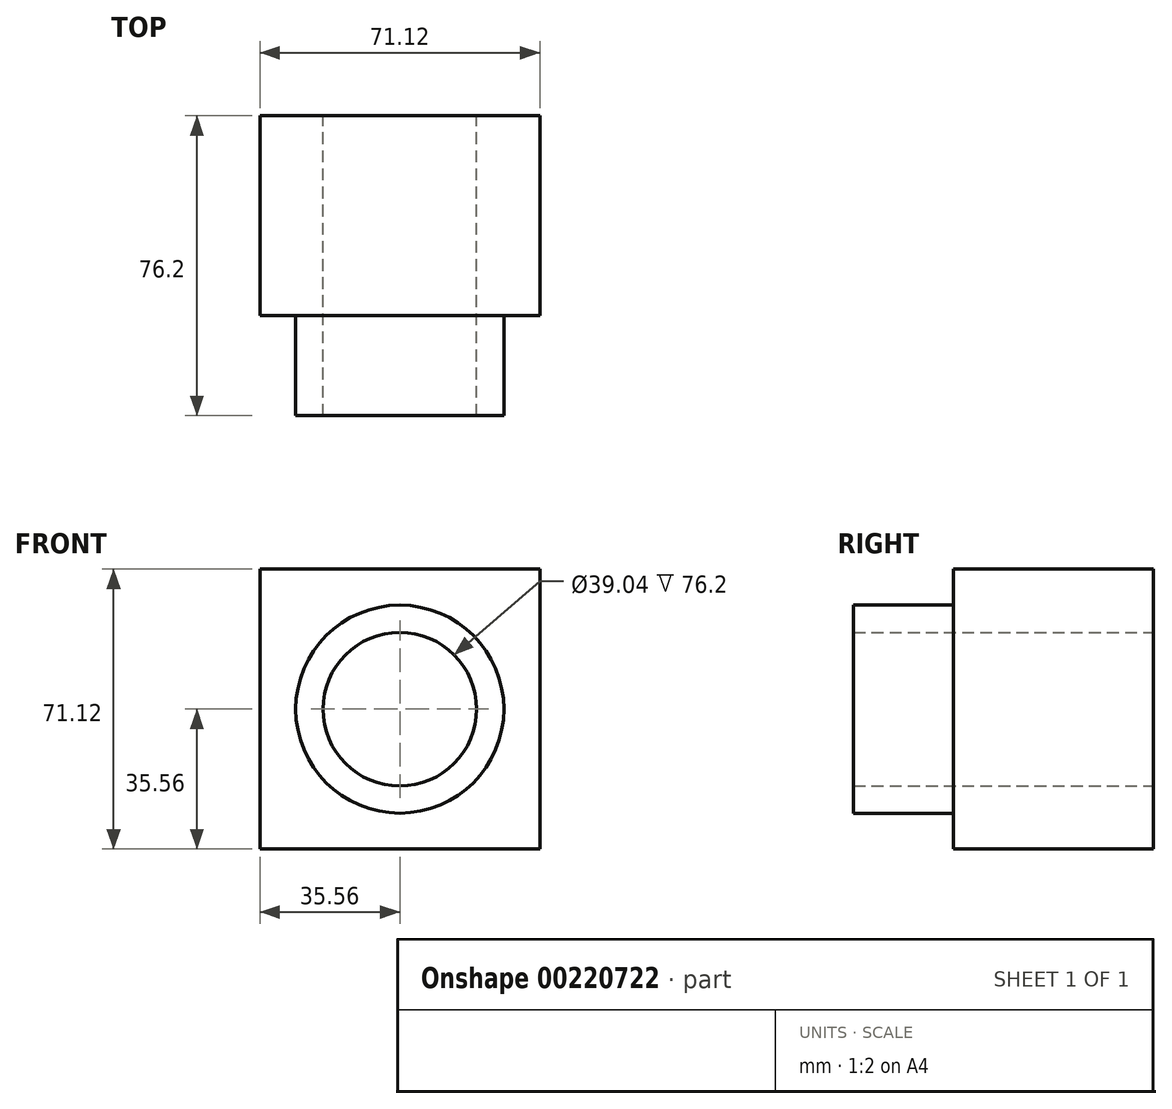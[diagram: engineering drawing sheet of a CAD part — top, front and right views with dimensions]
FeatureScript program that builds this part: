
annotation { "Feature Type Name" : "Feature", "Feature Type Description" : "" }
export const myFeature = defineFeature(function(context is Context, id is Id, definition is map)
    precondition{}
    {
        {
            var Q0;
            Q0=qCreatedBy(makeId("Front.planeOp"),FACE);
            var sketch = newSketch(context, id + "F0", { "sketchPlane" : qUnion([Q0])});
            skLineSegment(sketch, "E0.bottom", {"start": v(35.56, 35.56) * mm, "end": v(-35.56, 35.56) * mm});
            skLineSegment(sketch, "E0.top", {"start": v(35.56, -35.56) * mm, "end": v(-35.56, -35.56) * mm});
            skLineSegment(sketch, "E0.left", {"start": v(35.56, 35.56) * mm, "end": v(35.56, -35.56) * mm});
            skLineSegment(sketch, "E0.right", {"start": v(-35.56, 35.56) * mm, "end": v(-35.56, -35.56) * mm});
            skPoint(sketch, "E0.middle", {"position": v(0, 0) * mm});
            skCircle(sketch, "E1", {"center": v(0, 0) * mm, "radius": 19.52 * mm});
            skSolve(sketch);
        }
        {
            var Q0;
            Q0=makeQuery(id+"F0.imprint","IMPRINT",FACE,{"disambiguationData":[TD([[makeQuery(id+"F0.imprint","IMPRINT",EDGE,{"derivedFrom":sQuery(id+"F0.wireOp",EDGE,"E0.bottom")}),1.0]])]});
            extrude(context, id + "F1", {"entities" : qUnion([Q0]), "endBound" : BoundingType.SYMMETRIC, "depth" : 50.8 * mm});
        }
        {
            var Q0;
            Q0=makeQuery(id+"F1.opExtrude","CAP_FACE",FACE,{"disambiguationData":[OSD([sQuery(id+"F0.wireOp",EDGE,"E0.bottom"),sQuery(id+"F0.wireOp",EDGE,"E0.top"),sQuery(id+"F0.wireOp",EDGE,"E0.left"),sQuery(id+"F0.wireOp",EDGE,"E0.right"),sQuery(id+"F0.wireOp",EDGE,"E1")])],"isStart":false});
            var sketch = newSketch(context, id + "F2", { "sketchPlane" : qUnion([Q0])});
            skCircle(sketch, "E2", {"center": v(0, 0) * mm, "radius": 26.43 * mm});
            skSolve(sketch);
        }
        {
            var Q0;
            Q0=makeQuery(id+"F2.imprint","IMPRINT",FACE,{"disambiguationData":[TD([[makeQuery(id+"F2.imprint","IMPRINT",EDGE,{"derivedFrom":sQuery(id+"F2.wireOp",EDGE,"E2")}),1.0]])]});
            extrude(context, id + "F3", {"entities" : qUnion([Q0]), "operationType" : NewBodyOperationType.ADD, "depth" : 25.4 * mm});
        }
    });
